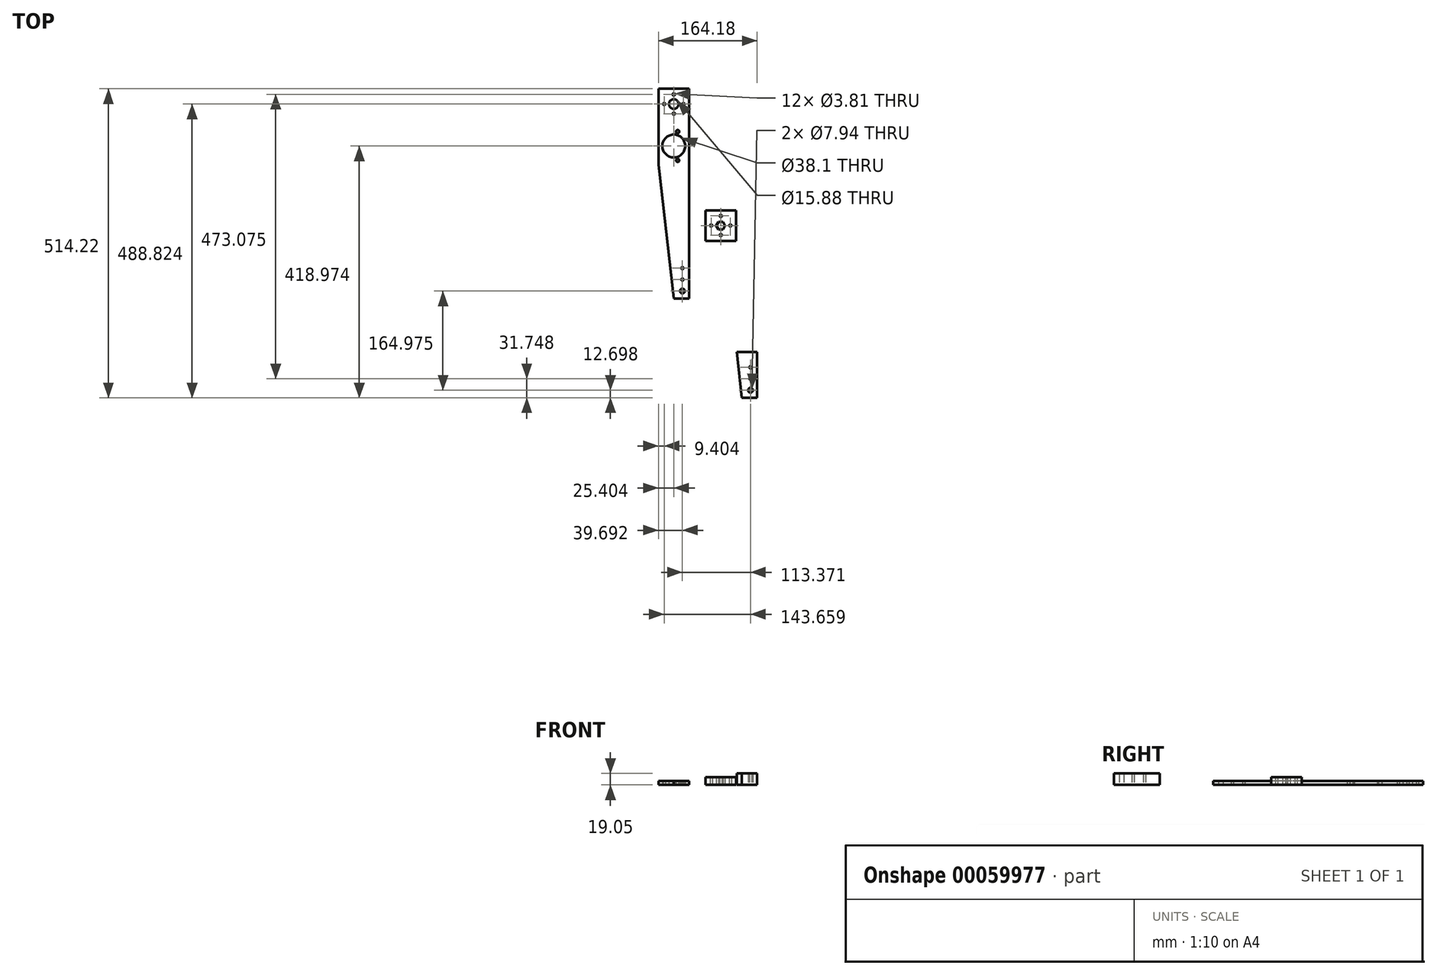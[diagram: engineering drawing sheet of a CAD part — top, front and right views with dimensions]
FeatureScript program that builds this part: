
annotation { "Feature Type Name" : "Feature", "Feature Type Description" : "" }
export const myFeature = defineFeature(function(context is Context, id is Id, definition is map)
    precondition{}
    {
        {
            var Q0;
            Q0=qCreatedBy(makeId("Top.planeOp"),FACE);
            var sketch = newSketch(context, id + "F0", { "sketchPlane" : qUnion([Q0])});
            skLineSegment(sketch, "E0.bottom", {"start": v(-78.13, 252.9) * mm, "end": v(-27.33, 252.9) * mm});
            skLineSegment(sketch, "E0.top", {"start": v(-78.13, 11.6) * mm, "end": v(-27.33, 11.6) * mm});
            skLineSegment(sketch, "E0.left", {"start": v(-78.13, 252.9) * mm, "end": v(-78.13, 11.6) * mm});
            skLineSegment(sketch, "E0.right", {"start": v(-27.33, 252.9) * mm, "end": v(-27.33, 11.6) * mm});
            skCircle(sketch, "E1", {"center": v(-52.73, 227.5) * mm, "radius": 7.94 * mm});
            skPoint(sketch, "E1.centerSnap0", {"position": v(-52.73, 252.9) * mm});
            skCircle(sketch, "E2", {"center": v(-52.73, 157.64) * mm, "radius": 19.05 * mm});
            skLineSegment(sketch, "E3.top", {"start": v(-78.13, -96.36) * mm, "end": v(-27.33, -96.36) * mm});
            skLineSegment(sketch, "E3.left", {"start": v(-78.13, 11.6) * mm, "end": v(-78.13, -96.36) * mm});
            skLineSegment(sketch, "E3.right", {"start": v(-27.33, 11.6) * mm, "end": v(-27.33, -96.36) * mm});
            skCircle(sketch, "E4", {"center": v(-52.73, 243.5) * mm, "radius": 1.9 * mm});
            skLineSegment(sketch, "E5", {"start": v(-52.73, 157.64) * mm, "end": v(-27.33, 157.64) * mm, "construction": true});
            skCircle(sketch, "E6", {"center": v(-46.23, 181.64) * mm, "radius": 2.7 * mm});
            skCircle(sketch, "E7.MirrorC", {"center": v(-46.23, 133.64) * mm, "radius": 2.7 * mm});
            skCircle(sketch, "E8.MirrorC", {"center": v(-38.44, -83.66) * mm, "radius": 3.97 * mm});
            skCircle(sketch, "E9.1.0", {"center": v(-68.73, 227.5) * mm, "radius": 1.9 * mm});
            skCircle(sketch, "E9.2.0", {"center": v(-52.73, 211.5) * mm, "radius": 1.9 * mm});
            skCircle(sketch, "E9.3.0", {"center": v(-36.73, 227.5) * mm, "radius": 1.9 * mm});
            skLineSegment(sketch, "E10", {"start": v(-78.13, 126.58) * mm, "end": v(-52.73, -96.36) * mm});
            skCircle(sketch, "E11", {"center": v(-38.44, -64.6) * mm, "radius": 1.9 * mm});
            skCircle(sketch, "E12", {"center": v(-38.44, -45.56) * mm, "radius": 1.9 * mm});
            skSolve(sketch);
        }
        {
            var Q0;
            {var subQ0=sQuery(id+"F0.wireOp",EDGE,"E3.right");Q0=makeQuery(id+"F0.imprint","IMPRINT",FACE,{"disambiguationData":[TD([[makeQuery(id+"F0.imprint","IMPRINT",EDGE,{"derivedFrom":subQ0}),-1.0]])]});}
            var Q1;
            {var subQ6=sQuery(id+"F0.wireOp",EDGE,"E0.bottom");Q1=makeQuery(id+"F0.imprint","IMPRINT",FACE,{"disambiguationData":[TD([[makeQuery(id+"F0.imprint","IMPRINT",EDGE,{"derivedFrom":subQ6}),-1.0]])]});}
            extrude(context, id + "F1", {"entities" : qUnion([Q0, Q1]), "depth" : 6.35 * mm});
        }
        {
            var Q0;
            Q0=qCreatedBy(makeId("Top.planeOp"),FACE);
            var sketch = newSketch(context, id + "F2", { "sketchPlane" : qUnion([Q0])});
            skLineSegment(sketch, "E13.bottom", {"start": v(0, 0) * mm, "end": v(50.8, 0) * mm});
            skLineSegment(sketch, "E13.top", {"start": v(0, 50.8) * mm, "end": v(50.8, 50.8) * mm});
            skLineSegment(sketch, "E13.left", {"start": v(0, 0) * mm, "end": v(0, 50.8) * mm});
            skLineSegment(sketch, "E13.right", {"start": v(50.8, 0) * mm, "end": v(50.8, 50.8) * mm});
            skCircle(sketch, "E14.cCircle", {"center": v(25.4, 25.4) * mm, "radius": 6.35 * mm, "construction": true});
            skPoint(sketch, "E14.cCircle.centerSnap0", {"position": v(0, 25.4) * mm});
            skPoint(sketch, "E14.cCircle.centerSnap1", {"position": v(25.4, 0) * mm});
            skLineSegment(sketch, "E14.0", {"start": v(21.73, 31.75) * mm, "end": v(29.07, 31.75) * mm});
            skLineSegment(sketch, "E14.1", {"start": v(29.07, 31.75) * mm, "end": v(32.73, 25.4) * mm});
            skLineSegment(sketch, "E14.2", {"start": v(32.73, 25.4) * mm, "end": v(29.07, 19.05) * mm});
            skLineSegment(sketch, "E14.3", {"start": v(29.07, 19.05) * mm, "end": v(21.73, 19.05) * mm});
            skLineSegment(sketch, "E14.4", {"start": v(21.73, 19.05) * mm, "end": v(18.07, 25.4) * mm});
            skLineSegment(sketch, "E14.5", {"start": v(18.07, 25.4) * mm, "end": v(21.73, 31.75) * mm});
            skPoint(sketch, "E14.0.midPoint", {"position": v(25.4, 31.75) * mm});
            skCircle(sketch, "E15", {"center": v(25.4, 41.4) * mm, "radius": 1.9 * mm});
            skCircle(sketch, "E16.1.0", {"center": v(9.4, 25.4) * mm, "radius": 1.9 * mm});
            skCircle(sketch, "E16.2.0", {"center": v(25.4, 9.4) * mm, "radius": 1.9 * mm});
            skCircle(sketch, "E16.3.0", {"center": v(41.4, 25.4) * mm, "radius": 1.9 * mm});
            skSolve(sketch);
        }
        {
            var Q0;
            Q0=makeQuery(id+"F2.imprint","IMPRINT",FACE,{"disambiguationData":[TD([[makeQuery(id+"F2.imprint","IMPRINT",EDGE,{"derivedFrom":sQuery(id+"F2.wireOp",EDGE,"E13.bottom")}),1.0]])]});
            extrude(context, id + "F3", {"entities" : qUnion([Q0]), "depth" : 12.7 * mm});
        }
        {
            var Q0;
            Q0=qCreatedBy(makeId("Top.planeOp"),FACE);
            var sketch = newSketch(context, id + "F4", { "sketchPlane" : qUnion([Q0])});
            skLineSegment(sketch, "E17.bottom", {"start": v(35.25, -261.33) * mm, "end": v(86.05, -261.33) * mm});
            skLineSegment(sketch, "E17.top", {"start": v(35.25, -185.13) * mm, "end": v(86.05, -185.13) * mm});
            skLineSegment(sketch, "E17.left", {"start": v(35.25, -261.33) * mm, "end": v(35.25, -185.13) * mm});
            skLineSegment(sketch, "E17.right", {"start": v(86.05, -261.33) * mm, "end": v(86.05, -185.13) * mm});
            skCircle(sketch, "E18", {"center": v(74.93, -248.63) * mm, "radius": 3.97 * mm});
            skCircle(sketch, "E19", {"center": v(74.93, -229.58) * mm, "radius": 1.9 * mm});
            skCircle(sketch, "E20", {"center": v(74.93, -210.53) * mm, "radius": 1.9 * mm});
            skLineSegment(sketch, "E21", {"start": v(60.65, -261.33) * mm, "end": v(51.96, -185.13) * mm});
            skSolve(sketch);
        }
        {
            var Q0;
            {var subQ0=sQuery(id+"F4.wireOp",EDGE,"E17.right");Q0=makeQuery(id+"F4.imprint","IMPRINT",FACE,{"disambiguationData":[TD([[makeQuery(id+"F4.imprint","IMPRINT",EDGE,{"derivedFrom":subQ0}),1.0]])]});}
            extrude(context, id + "F5", {"entities" : qUnion([Q0]), "depth" : 19.05 * mm});
        }
    });
